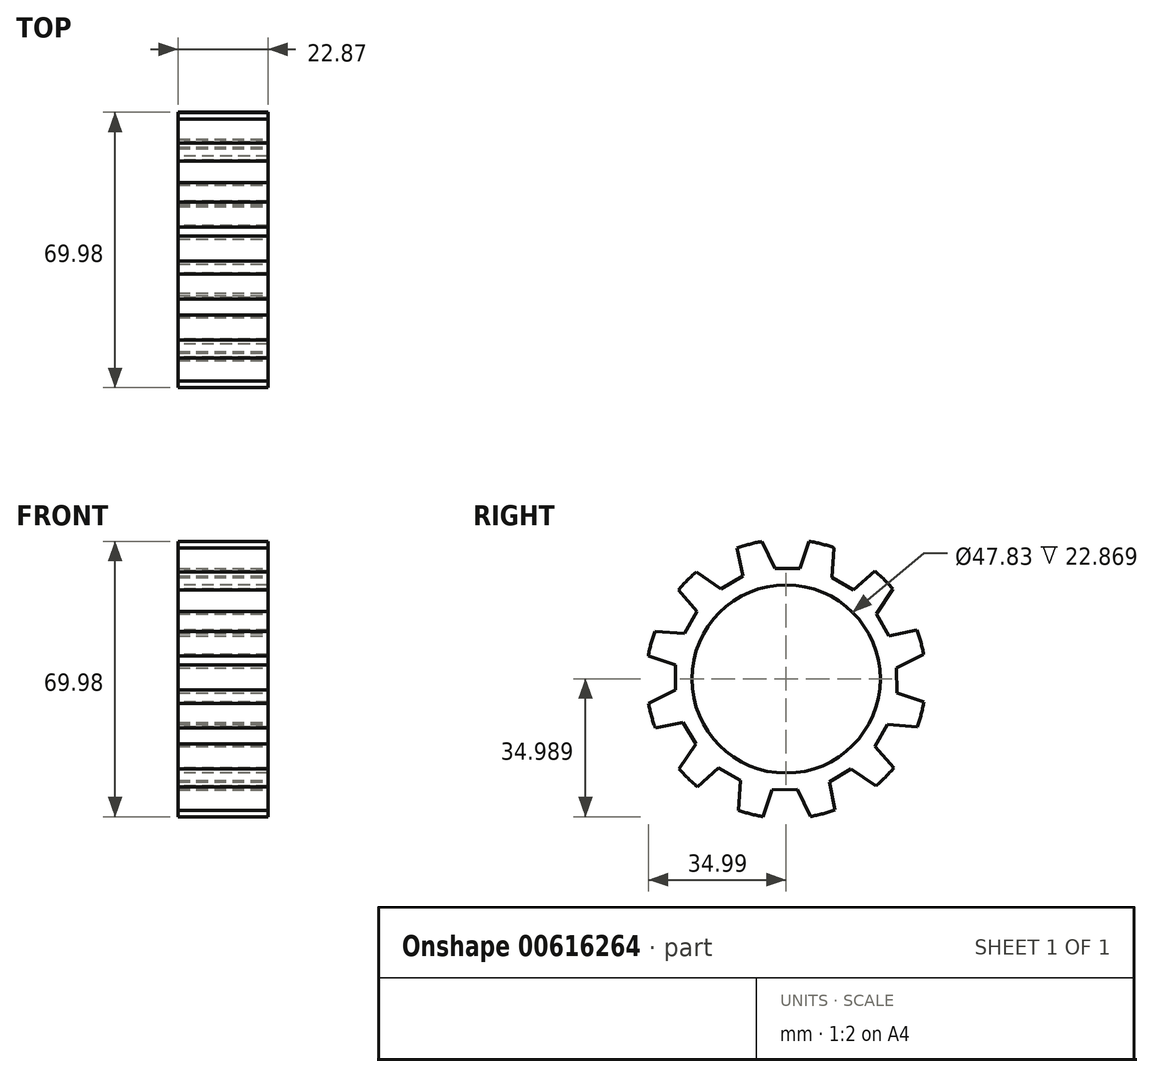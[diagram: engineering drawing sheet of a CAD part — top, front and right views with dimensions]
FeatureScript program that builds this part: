
annotation { "Feature Type Name" : "Feature", "Feature Type Description" : "" }
export const myFeature = defineFeature(function(context is Context, id is Id, definition is map)
    precondition{}
    {
        {
            var Q0;
            Q0=qCreatedBy(makeId("Front.planeOp"),FACE);
            var sketch = newSketch(context, id + "F0", { "sketchPlane" : qUnion([Q0])});
            skLineSegment(sketch, "E0.bottom", {"start": v(-10.45, 53.37) * mm, "end": v(12.42, 53.37) * mm});
            skLineSegment(sketch, "E0.top", {"start": v(-10.45, 41.81) * mm, "end": v(12.42, 41.81) * mm});
            skLineSegment(sketch, "E0.left", {"start": v(-10.45, 53.37) * mm, "end": v(-10.45, 41.81) * mm});
            skLineSegment(sketch, "E0.right", {"start": v(12.42, 53.37) * mm, "end": v(12.42, 41.81) * mm});
            skLineSegment(sketch, "E1.bottom", {"start": v(-5.55, 41.81) * mm, "end": v(7.45, 41.81) * mm});
            skLineSegment(sketch, "E1.top", {"start": v(-5.55, 30.58) * mm, "end": v(7.45, 30.58) * mm});
            skLineSegment(sketch, "E1.left", {"start": v(-5.55, 41.81) * mm, "end": v(-5.55, 30.58) * mm});
            skLineSegment(sketch, "E1.right", {"start": v(7.45, 41.81) * mm, "end": v(7.45, 30.58) * mm});
            skLineSegment(sketch, "E2", {"start": v(-21.75, 17.9) * mm, "end": v(25.67, 17.9) * mm});
            skSolve(sketch);
        }
        {
            var Q0;
            Q0=makeQuery(id+"F0.imprint","IMPRINT",FACE,{"disambiguationData":[TD([[makeQuery(id+"F0.imprint","IMPRINT",EDGE,{"derivedFrom":sQuery(id+"F0.wireOp",EDGE,"E0.bottom")}),-1.0]])]});
            var Q1;
            Q1=makeQuery(id+"F0.imprint","IMPRINT",FACE,{"disambiguationData":[TD([[makeQuery(id+"F0.imprint","IMPRINT",EDGE,{"derivedFrom":sQuery(id+"F0.wireOp",EDGE,"E1.bottom")}),-1.0]])]});
            var Q2;
            Q2=sQuery(id+"F0.wireOp",EDGE,"E2");
            revolve(context, id + "F1", {"entities" : qUnion([Q0, Q1]), "axis" : qUnion([Q2]), "revolveType" : RevolveType.FULL});
        }
        {
            var Q0;
            Q0=qCreatedBy(makeId("Right.planeOp"),FACE);
            var sketch = newSketch(context, id + "F2", { "sketchPlane" : qUnion([Q0])});
            skLineSegment(sketch, "E3", {"start": v(-6.97, 54.48) * mm, "end": v(-2.84, 46) * mm});
            skLineSegment(sketch, "E4", {"start": v(-2.84, 46) * mm, "end": v(3.56, 46.03) * mm});
            skLineSegment(sketch, "E5", {"start": v(3.56, 46.03) * mm, "end": v(6.66, 55.33) * mm});
            skLineSegment(sketch, "E6", {"start": v(6.66, 55.33) * mm, "end": v(-6.97, 54.48) * mm});
            skSolve(sketch);
        }
        {
            var Q0;
            Q0 = qSketchRegion(id + "F2", true);
            extrude(context, id + "F3", {"entities" : qUnion([Q0]), "operationType" : NewBodyOperationType.REMOVE, "endBound" : BoundingType.SYMMETRIC, "oppositeDirection" : true, "depth" : 71.1 * mm, "offsetDistance" : 25.4 * mm});
        }
        {
            var Q0;
            Q0=makeQuery(id+"F3.boolean.opBoolean","COPY",FACE,{"derivedFrom":makeQuery(id+"F3.opExtrude","SWEPT_FACE",FACE,{"disambiguationData":[OSD([sQuery(id+"F2.wireOp",EDGE,"E5")])]})});
            var Q1;
            Q1=makeQuery(id+"F3.boolean.opBoolean","COPY",FACE,{"derivedFrom":makeQuery(id+"F3.opExtrude","SWEPT_FACE",FACE,{"disambiguationData":[OSD([sQuery(id+"F2.wireOp",EDGE,"E3")])]})});
            var Q2;
            Q2=makeQuery(id+"F3.boolean.opBoolean","COPY",FACE,{"derivedFrom":makeQuery(id+"F3.opExtrude","SWEPT_FACE",FACE,{"disambiguationData":[OSD([sQuery(id+"F2.wireOp",EDGE,"E4")])]})});
            var Q3;
            Q3=makeQuery(id+"F1.opRevolve","SWEPT_EDGE",EDGE,{"disambiguationData":[OSD([sQuery(id+"F0.wireOp",EDGE,"E0.bottom"),sQuery(id+"F0.wireOp",EDGE,"E0.right")])]});
            circularPattern(context, id + "F4", {"patternType" : PatternType.FACE, "faces" : qUnion([Q0, Q1, Q2]), "axis" : qUnion([Q3]), "angle" : 360 * degree, "instanceCount" : 12, "equalSpace" : true});
        }
    });
